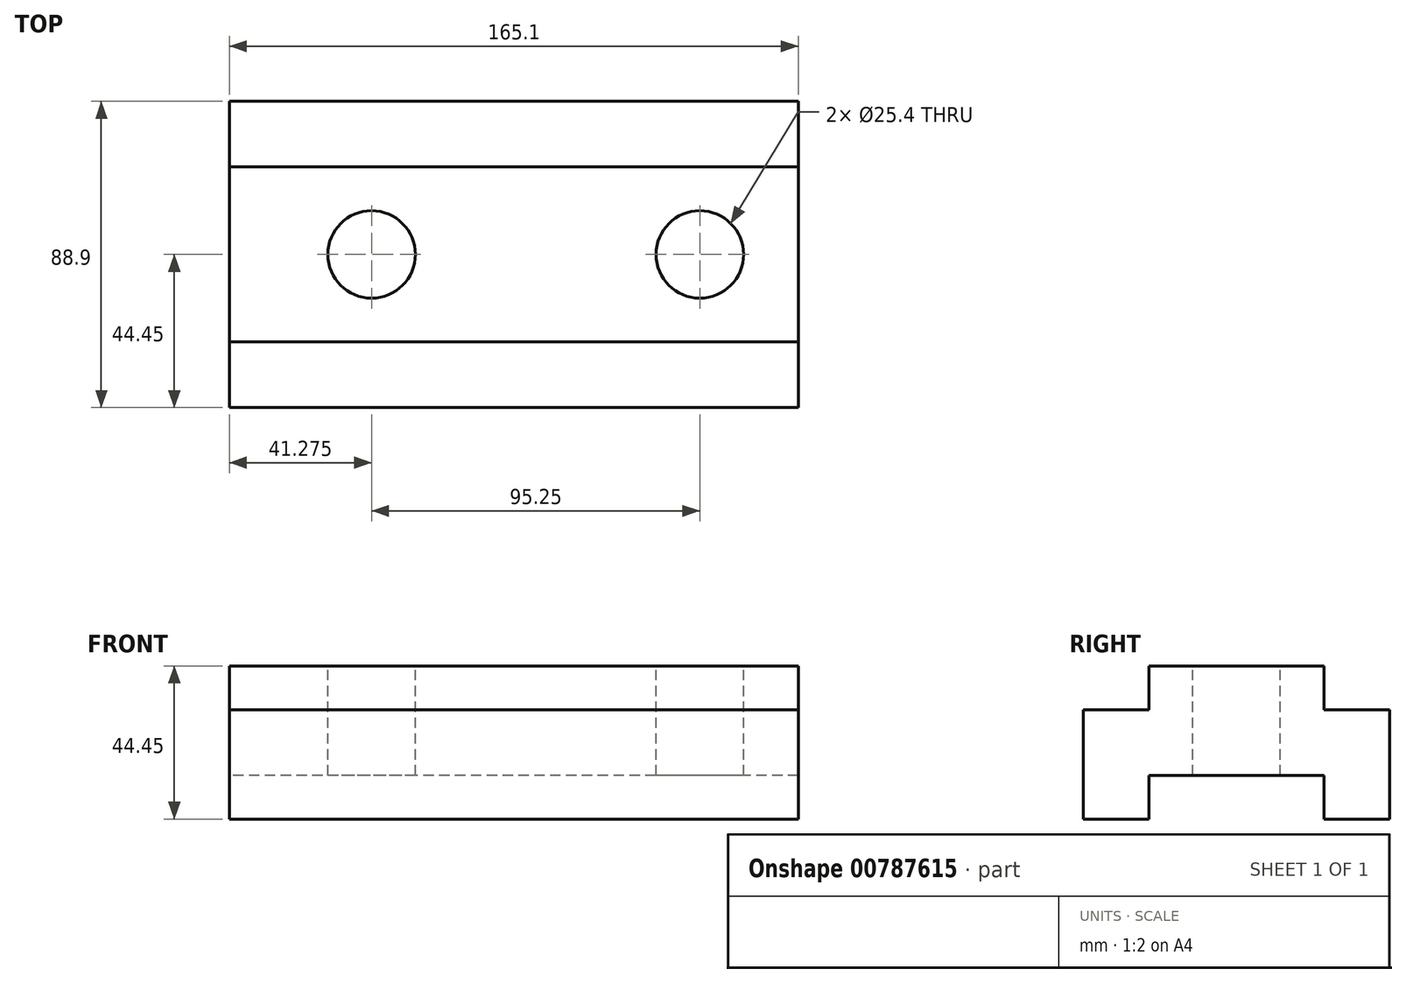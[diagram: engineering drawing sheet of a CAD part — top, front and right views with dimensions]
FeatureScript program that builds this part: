
annotation { "Feature Type Name" : "Feature", "Feature Type Description" : "" }
export const myFeature = defineFeature(function(context is Context, id is Id, definition is map)
    precondition{}
    {
        {
            var Q0;
            Q0=qCreatedBy(makeId("Right.planeOp"),FACE);
            var sketch = newSketch(context, id + "F0", { "sketchPlane" : qUnion([Q0])});
            skLineSegment(sketch, "E0", {"start": v(0, 0) * mm, "end": v(19.05, 0) * mm});
            skLineSegment(sketch, "E1", {"start": v(19.05, 0) * mm, "end": v(19.05, 12.7) * mm});
            skLineSegment(sketch, "E2", {"start": v(19.05, 12.7) * mm, "end": v(69.85, 12.7) * mm});
            skLineSegment(sketch, "E3", {"start": v(69.85, 12.7) * mm, "end": v(69.85, 0) * mm});
            skLineSegment(sketch, "E4", {"start": v(69.85, 0) * mm, "end": v(88.9, 0) * mm});
            skLineSegment(sketch, "E5", {"start": v(88.9, 0) * mm, "end": v(88.9, 31.75) * mm});
            skLineSegment(sketch, "E6", {"start": v(88.9, 31.75) * mm, "end": v(69.85, 31.75) * mm});
            skLineSegment(sketch, "E7", {"start": v(69.85, 31.75) * mm, "end": v(69.85, 44.45) * mm});
            skLineSegment(sketch, "E8", {"start": v(69.85, 44.45) * mm, "end": v(19.05, 44.45) * mm});
            skLineSegment(sketch, "E9", {"start": v(19.05, 44.45) * mm, "end": v(19.05, 31.75) * mm});
            skLineSegment(sketch, "E10", {"start": v(19.05, 31.75) * mm, "end": v(0, 31.75) * mm});
            skLineSegment(sketch, "E11", {"start": v(0, 31.75) * mm, "end": v(0, 0) * mm});
            skSolve(sketch);
        }
        {
            var Q0;
            Q0=makeQuery(id+"F0.imprint","IMPRINT",FACE,{"disambiguationData":[TD([[makeQuery(id+"F0.imprint","IMPRINT",EDGE,{"derivedFrom":sQuery(id+"F0.wireOp",EDGE,"E0")}),1.0]])]});
            extrude(context, id + "F1", {"entities" : qUnion([Q0]), "depth" : 165.1 * mm, "offsetDistance" : 25.4 * mm});
        }
        {
            var Q0;
            Q0=makeQuery(id+"F1.opExtrude","SWEPT_FACE",FACE,{"disambiguationData":[OSD([sQuery(id+"F0.wireOp",EDGE,"E8")])]});
            var sketch = newSketch(context, id + "F2", { "sketchPlane" : qUnion([Q0])});
            skLineSegment(sketch, "E12", {"start": v(0, 44.45) * mm, "end": v(41.28, 44.45) * mm, "construction": true});
            skLineSegment(sketch, "E13", {"start": v(41.28, 44.45) * mm, "end": v(136.53, 44.45) * mm, "construction": true});
            skCircle(sketch, "E14", {"center": v(41.28, 44.45) * mm, "radius": 12.7 * mm});
            skCircle(sketch, "E15", {"center": v(136.53, 44.45) * mm, "radius": 12.7 * mm});
            skSolve(sketch);
        }
        {
            var Q0;
            Q0 = qSketchRegion(id + "F2", true);
            extrude(context, id + "F3", {"entities" : qUnion([Q0]), "operationType" : NewBodyOperationType.REMOVE, "endBound" : BoundingType.THROUGH_ALL, "oppositeDirection" : true, "depth" : 25.4 * mm, "offsetDistance" : 25.4 * mm});
        }
    });
